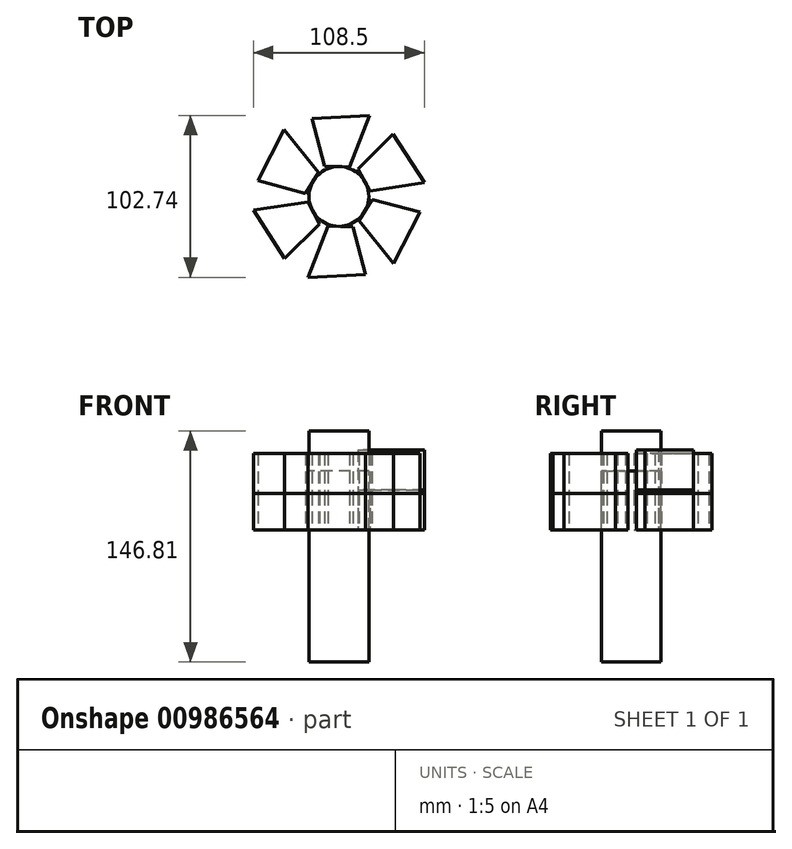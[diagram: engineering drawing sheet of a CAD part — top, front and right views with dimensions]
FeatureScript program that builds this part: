
annotation { "Feature Type Name" : "Feature", "Feature Type Description" : "" }
export const myFeature = defineFeature(function(context is Context, id is Id, definition is map)
    precondition{}
    {
        {
            var Q0;
            Q0=qCreatedBy(makeId("Top.planeOp"),FACE);
            var sketch = newSketch(context, id + "F0", { "sketchPlane" : qUnion([Q0])});
            skCircle(sketch, "E0", {"center": v(0, 0) * mm, "radius": 19 * mm});
            skLineSegment(sketch, "E1", {"start": v(12.23, 17.41) * mm, "end": v(19.66, 3.53) * mm});
            skLineSegment(sketch, "E2", {"start": v(19.66, 3.53) * mm, "end": v(54.25, 8.78) * mm});
            skLineSegment(sketch, "E3", {"start": v(54.25, 8.78) * mm, "end": v(34.4, 39.57) * mm});
            skLineSegment(sketch, "E4", {"start": v(34.4, 39.57) * mm, "end": v(12.23, 17.41) * mm});
            skLineSegment(sketch, "E5.1.0", {"start": v(-17.08, 49.57) * mm, "end": v(-8.96, 19.3) * mm});
            skLineSegment(sketch, "E5.1.1", {"start": v(19.52, 51.37) * mm, "end": v(-17.08, 49.57) * mm});
            skLineSegment(sketch, "E5.1.2", {"start": v(6.77, 18.79) * mm, "end": v(19.52, 51.37) * mm});
            skLineSegment(sketch, "E5.1.3", {"start": v(-8.96, 19.3) * mm, "end": v(6.77, 18.79) * mm});
            skLineSegment(sketch, "E5.2.0", {"start": v(-51.47, 10) * mm, "end": v(-21.2, 1.89) * mm});
            skLineSegment(sketch, "E5.2.1", {"start": v(-34.73, 42.6) * mm, "end": v(-51.47, 10) * mm});
            skLineSegment(sketch, "E5.2.2", {"start": v(-12.88, 15.26) * mm, "end": v(-34.73, 42.6) * mm});
            skLineSegment(sketch, "E5.2.3", {"start": v(-21.2, 1.89) * mm, "end": v(-12.88, 15.26) * mm});
            skLineSegment(sketch, "E5.3.0", {"start": v(-34.4, -39.57) * mm, "end": v(-12.23, -17.41) * mm});
            skLineSegment(sketch, "E5.3.1", {"start": v(-54.25, -8.78) * mm, "end": v(-34.4, -39.57) * mm});
            skLineSegment(sketch, "E5.3.2", {"start": v(-19.66, -3.53) * mm, "end": v(-54.25, -8.78) * mm});
            skLineSegment(sketch, "E5.3.3", {"start": v(-12.23, -17.41) * mm, "end": v(-19.66, -3.53) * mm});
            skLineSegment(sketch, "E5.4.0", {"start": v(17.08, -49.57) * mm, "end": v(8.96, -19.3) * mm});
            skLineSegment(sketch, "E5.4.1", {"start": v(-19.52, -51.37) * mm, "end": v(17.08, -49.57) * mm});
            skLineSegment(sketch, "E5.4.2", {"start": v(-6.77, -18.79) * mm, "end": v(-19.52, -51.37) * mm});
            skLineSegment(sketch, "E5.4.3", {"start": v(8.96, -19.3) * mm, "end": v(-6.77, -18.79) * mm});
            skLineSegment(sketch, "E5.5.0", {"start": v(51.47, -10) * mm, "end": v(21.2, -1.89) * mm});
            skLineSegment(sketch, "E5.5.1", {"start": v(34.73, -42.6) * mm, "end": v(51.47, -10) * mm});
            skLineSegment(sketch, "E5.5.2", {"start": v(12.88, -15.26) * mm, "end": v(34.73, -42.6) * mm});
            skLineSegment(sketch, "E5.5.3", {"start": v(21.2, -1.89) * mm, "end": v(12.88, -15.26) * mm});
            skSolve(sketch);
        }
        {
            var Q0;
            {var subQ0=sQuery(id+"F0.wireOp",EDGE,"E0");var subQ4=makeQuery(id+"F0.imprint","INTERSECT",VERTEX,{"derivedFrom":[subQ0,sQuery(id+"F0.wireOp",EDGE,"E5.1.3")]});Q0=makeQuery(id+"F0.imprint","IMPRINT",FACE,{"disambiguationData":[TD([[makeQuery(id+"F0.imprint","IMPRINT",EDGE,{"disambiguationData":[TD([[subQ4,1.0]])],"derivedFrom":subQ0}),1.0]])]});}
            extrude(context, id + "F1", {"entities" : qUnion([Q0]), "oppositeDirection" : true, "depth" : 83.82 * mm, "offsetDistance" : 25.4 * mm});
        }
        {
            var Q0;
            Q0=makeQuery(id+"F1.opExtrude","CAP_FACE",FACE,{"disambiguationData":[OSD([sQuery(id+"F0.wireOp",EDGE,"E0")])],"isStart":true});
            extrude(context, id + "F2", {"entities" : qUnion([Q0]), "operationType" : NewBodyOperationType.ADD, "depth" : 14.48 * mm, "offsetDistance" : 25.4 * mm});
        }
        {
            var Q0;
            Q0 = qSketchRegion(id + "F0", true);
            var Q1;
            Q1=makeQuery(id+"F2.opExtrude","CAP_FACE",FACE,{"disambiguationData":[OSD([sQuery(id+"F0.wireOp",EDGE,"E0")])],"isStart":false});
            extrude(context, id + "F3", {"entities" : qUnion([Q0, Q1]), "operationType" : NewBodyOperationType.ADD, "depth" : 23.1 * mm, "offsetDistance" : 25.4 * mm});
        }
        {
            var Q0;
            {var subQ0=sQuery(id+"F0.wireOp",EDGE,"E2");Q0=makeQuery(id+"F0.imprint","IMPRINT",FACE,{"disambiguationData":[TD([[makeQuery(id+"F0.imprint","IMPRINT",EDGE,{"derivedFrom":subQ0}),1.0]])]});}
            extrude(context, id + "F4", {"entities" : qUnion([Q0]), "depth" : 25.4 * mm, "offsetDistance" : 25.4 * mm});
        }
        {
            var Q0;
            {var subQ0=sQuery(id+"F0.wireOp",EDGE,"E2");Q0=makeQuery(id+"F0.imprint","IMPRINT",FACE,{"disambiguationData":[TD([[makeQuery(id+"F0.imprint","IMPRINT",EDGE,{"derivedFrom":subQ0}),1.0]])]});}
            var Q1;
            Q1=makeQuery(id+"F3.opExtrude","CAP_FACE",FACE,{"disambiguationData":[OSD([sQuery(id+"F0.wireOp",EDGE,"E5.4.0"),sQuery(id+"F0.wireOp",EDGE,"E5.4.1"),sQuery(id+"F0.wireOp",EDGE,"E5.4.2"),sQuery(id+"F0.wireOp",EDGE,"E5.4.3")])],"isStart":false});
            var Q2;
            Q2=makeQuery(id+"F3.opExtrude","CAP_FACE",FACE,{"disambiguationData":[OSD([sQuery(id+"F0.wireOp",EDGE,"E5.5.0"),sQuery(id+"F0.wireOp",EDGE,"E5.5.1"),sQuery(id+"F0.wireOp",EDGE,"E5.5.2"),sQuery(id+"F0.wireOp",EDGE,"E5.5.3")])],"isStart":false});
            var Q3;
            Q3=makeQuery(id+"F3.opExtrude","CAP_FACE",FACE,{"disambiguationData":[OSD([sQuery(id+"F0.wireOp",EDGE,"E5.3.0"),sQuery(id+"F0.wireOp",EDGE,"E5.3.1"),sQuery(id+"F0.wireOp",EDGE,"E5.3.2"),sQuery(id+"F0.wireOp",EDGE,"E5.3.3")])],"isStart":false});
            var Q4;
            {var subQ0=sQuery(id+"F0.wireOp",EDGE,"E0");Q4=makeQuery(id+"F3.opExtrude","CAP_FACE",FACE,{"disambiguationData":[OSD([subQ0]),TDD([makeQuery(id+"F2.opExtrude","CAP_FACE",FACE,{"disambiguationData":[OSD([subQ0])],"isStart":false})])],"isStart":false});}
            var Q5;
            Q5=makeQuery(id+"F3.opExtrude","CAP_FACE",FACE,{"disambiguationData":[OSD([sQuery(id+"F0.wireOp",EDGE,"E5.2.0"),sQuery(id+"F0.wireOp",EDGE,"E5.2.1"),sQuery(id+"F0.wireOp",EDGE,"E5.2.2"),sQuery(id+"F0.wireOp",EDGE,"E5.2.3")])],"isStart":false});
            var Q6;
            Q6=makeQuery(id+"F3.opExtrude","CAP_FACE",FACE,{"disambiguationData":[OSD([sQuery(id+"F0.wireOp",EDGE,"E5.1.0"),sQuery(id+"F0.wireOp",EDGE,"E5.1.1"),sQuery(id+"F0.wireOp",EDGE,"E5.1.2"),sQuery(id+"F0.wireOp",EDGE,"E5.1.3")])],"isStart":false});
            extrude(context, id + "F5", {"entities" : qUnion([Q0, Q1, Q2, Q3, Q4, Q5, Q6]), "depth" : 25.4 * mm, "offsetDistance" : 25.4 * mm});
        }
        {
            var Q0;
            Q0=makeQuery(id+"F4.opExtrude","CAP_FACE",FACE,{"disambiguationData":[OSD([sQuery(id+"F0.wireOp",EDGE,"E1"),sQuery(id+"F0.wireOp",EDGE,"E2"),sQuery(id+"F0.wireOp",EDGE,"E3"),sQuery(id+"F0.wireOp",EDGE,"E4")])],"isStart":false});
            extrude(context, id + "F6", {"entities" : qUnion([Q0]), "depth" : 25.4 * mm, "offsetDistance" : 25.4 * mm});
        }
    });
